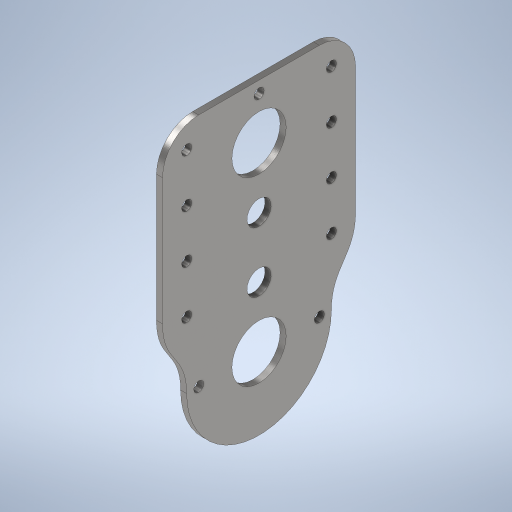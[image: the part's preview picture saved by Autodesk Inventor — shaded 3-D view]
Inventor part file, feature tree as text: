
AUTODESK INVENTOR PART (.ipt)
format: ipt  version: 2024 (Build 280153000, 153)  size: 343,040 bytes
history: native  units: in
note: dims shown in document units (in); Inventor stores cm internally (conversion verified against a paired STEP export)
features: extrude x2, fillet x1, sketch x1
ambient origin geometry x8: Origin, YZ Plane, XZ Plane, XY Plane, X Axis, Y Axis, Z Axis, Center Point
bodies: Solid1 (feature_tree)
feature tree (4):
  extrude  "Extrusion1"  Depth=0.75in
  fillet  "Fillet3"  Radius=1.125in
  extrude  "Extrusion2"  Depth=0.75in
  sketch  "Sketch3"  dims[d0=4.0in d1=6.0in d2=1.125in d3=0.5in d4=0.5in d5=1.125in d6=1.25in d7=1.25in d8=1.25in d9=0.2087in d10=0.5in d11=0.5in d12=2.3622in d14=1.0in d15=0.7874in d17=3.0in d20=0.125in d21=0.0in d22=0.5in d24=7.2441in d25=1.0in d26=2.0in d27=135.0deg d30=0.75in d31=2.0in d32=3.0in d33=1.25in d34=1.25in d35=0.75in d36=0.75in d37=0.7874in d39=90.0deg d41=1.25in d43=0.24in d44=0.21in d45=1.0in d46=0.0in d23=0.0344in]
